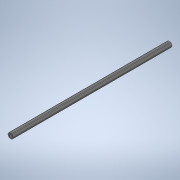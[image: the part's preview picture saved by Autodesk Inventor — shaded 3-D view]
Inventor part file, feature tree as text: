
AUTODESK INVENTOR PART (.ipt)
format: ipt  version: 2020 (Build 240168000, 168)  size: 137,216 bytes
history: native  units: in
note: dims shown in document units (in); Inventor stores cm internally (conversion verified against a paired STEP export)
features: plane x1, extrude x1, sketch x1, other x1
ambient origin geometry x8: Origin, YZ Plane, XZ Plane, XY Plane, X Axis, Y Axis, Z Axis, Center Point
bodies: Solid1 (feature_tree)
feature tree (4):
  plane  "Work Plane1"
  extrude  "Extrusion1"  Depth=1.0in
  sketch  "Sketch1"  dims[d0=-16.0in d1=1.0in d2=1.0in d3=2.0in d4=2.0in d5=27.0in d6=0.0in]
  other  "Cut-Extrude2"
